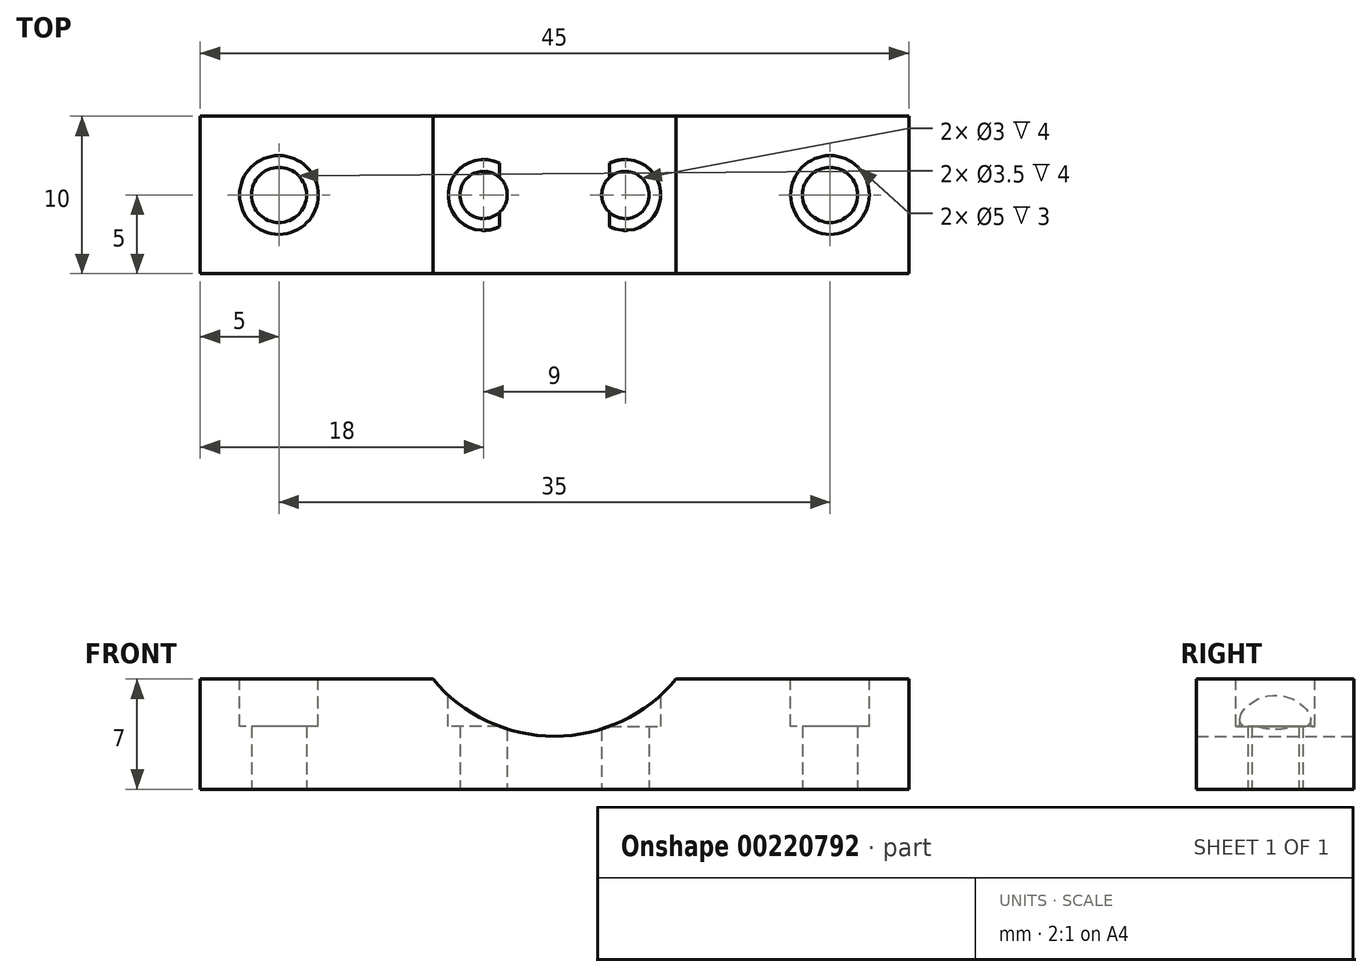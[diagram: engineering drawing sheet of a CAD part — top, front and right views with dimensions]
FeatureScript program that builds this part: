
annotation { "Feature Type Name" : "Feature", "Feature Type Description" : "" }
export const myFeature = defineFeature(function(context is Context, id is Id, definition is map)
    precondition{}
    {
        {
            var Q0;
            Q0=qCreatedBy(makeId("Top.planeOp"),FACE);
            var sketch = newSketch(context, id + "F0", { "sketchPlane" : qUnion([Q0])});
            skLineSegment(sketch, "E0.bottom", {"start": v(22.5, 5) * mm, "end": v(-22.5, 5) * mm});
            skLineSegment(sketch, "E0.top", {"start": v(22.5, -5) * mm, "end": v(-22.5, -5) * mm});
            skLineSegment(sketch, "E0.left", {"start": v(22.5, 5) * mm, "end": v(22.5, -5) * mm});
            skLineSegment(sketch, "E0.right", {"start": v(-22.5, 5) * mm, "end": v(-22.5, -5) * mm});
            skPoint(sketch, "E0.middle", {"position": v(0, 0) * mm});
            skCircle(sketch, "E1", {"center": v(-4.5, 0) * mm, "radius": 1.5 * mm});
            skCircle(sketch, "E2", {"center": v(4.5, 0) * mm, "radius": 1.5 * mm});
            skLineSegment(sketch, "E3", {"start": v(-22.5, 0) * mm, "end": v(-17.5, 0) * mm});
            skLineSegment(sketch, "E4", {"start": v(22.5, 0) * mm, "end": v(17.5, 0) * mm});
            skCircle(sketch, "E5", {"center": v(-17.5, 0) * mm, "radius": 1.75 * mm});
            skCircle(sketch, "E6", {"center": v(17.5, 0) * mm, "radius": 1.75 * mm});
            skSolve(sketch);
        }
        {
            var Q0;
            {var subQ3=sQuery(id+"F0.wireOp",EDGE,"E0.bottom");Q0=makeQuery(id+"F0.imprint","IMPRINT",FACE,{"disambiguationData":[TD([[makeQuery(id+"F0.imprint","IMPRINT",EDGE,{"derivedFrom":subQ3}),1.0]])]});}
            extrude(context, id + "F1", {"entities" : qUnion([Q0]), "depth" : 7 * mm});
        }
        {
            var Q0;
            Q0=makeQuery(id+"F1.opExtrude","CAP_FACE",FACE,{"disambiguationData":[OSD([sQuery(id+"F0.wireOp",EDGE,"E0.bottom"),sQuery(id+"F0.wireOp",EDGE,"E0.top"),sQuery(id+"F0.wireOp",EDGE,"E0.left"),sQuery(id+"F0.wireOp",EDGE,"E0.right"),sQuery(id+"F0.wireOp",EDGE,"E1"),sQuery(id+"F0.wireOp",EDGE,"E2"),sQuery(id+"F0.wireOp",EDGE,"E5"),sQuery(id+"F0.wireOp",EDGE,"E6")])],"isStart":false});
            var sketch = newSketch(context, id + "F2", { "sketchPlane" : qUnion([Q0])});
            skCircle(sketch, "E7", {"center": v(-17.5, 0) * mm, "radius": 2.5 * mm});
            skCircle(sketch, "E8", {"center": v(-4.5, 0) * mm, "radius": 2.25 * mm});
            skCircle(sketch, "E9", {"center": v(4.5, 0) * mm, "radius": 2.25 * mm});
            skCircle(sketch, "E10", {"center": v(17.5, 0) * mm, "radius": 2.5 * mm});
            skSolve(sketch);
        }
        {
            var Q0;
            Q0=makeQuery(id+"F2.imprint","IMPRINT",FACE,{"disambiguationData":[TD([[makeQuery(id+"F2.imprint","IMPRINT",EDGE,{"derivedFrom":sQuery(id+"F2.wireOp",EDGE,"E7")}),1.0]])]});
            var Q1;
            Q1=makeQuery(id+"F2.imprint","IMPRINT",FACE,{"disambiguationData":[TD([[makeQuery(id+"F2.imprint","IMPRINT",EDGE,{"derivedFrom":sQuery(id+"F2.wireOp",EDGE,"E8")}),1.0]])]});
            var Q2;
            Q2=makeQuery(id+"F2.imprint","IMPRINT",FACE,{"disambiguationData":[TD([[makeQuery(id+"F2.imprint","IMPRINT",EDGE,{"derivedFrom":sQuery(id+"F2.wireOp",EDGE,"E9")}),1.0]])]});
            var Q3;
            Q3=makeQuery(id+"F2.imprint","IMPRINT",FACE,{"disambiguationData":[TD([[makeQuery(id+"F2.imprint","IMPRINT",EDGE,{"derivedFrom":sQuery(id+"F2.wireOp",EDGE,"E10")}),1.0]])]});
            extrude(context, id + "F3", {"entities" : qUnion([Q0, Q1, Q2, Q3]), "operationType" : NewBodyOperationType.REMOVE, "oppositeDirection" : true, "depth" : 3 * mm});
        }
        {
            var Q0;
            Q0=makeQuery(id+"F1.opExtrude","SWEPT_FACE",FACE,{"disambiguationData":[OSD([sQuery(id+"F0.wireOp",EDGE,"E0.bottom")])]});
            var sketch = newSketch(context, id + "F4", { "sketchPlane" : qUnion([Q0])});
            skLineSegment(sketch, "E11", {"start": v(0, 7) * mm, "end": v(0, 13.42) * mm});
            skPoint(sketch, "E11.endSnap0", {"position": v(0, 7) * mm});
            skCircle(sketch, "E12", {"center": v(0, 13.42) * mm, "radius": 10.04 * mm});
            skSolve(sketch);
        }
        {
            var Q0;
            {var subQ1=makeQuery(id+"F1.opExtrude","CAP_EDGE",EDGE,{"disambiguationData":[OSD([sQuery(id+"F0.wireOp",EDGE,"E0.bottom")])],"isStart":false});var subQ4=makeQuery(id+"F4.imprint","IMPRINT",VERTEX,{"derivedFrom":subQ1});Q0=makeQuery(id+"F4.imprint","IMPRINT",FACE,{"disambiguationData":[TD([[makeQuery(id+"F4.imprint","IMPRINT",EDGE,{"disambiguationData":[TD([[subQ4,1.0]])],"derivedFrom":subQ1}),1.0]])]});}
            var Q1;
            {var subQ1=makeQuery(id+"F1.opExtrude","CAP_EDGE",EDGE,{"disambiguationData":[OSD([sQuery(id+"F0.wireOp",EDGE,"E0.bottom")])],"isStart":false});var subQ4=makeQuery(id+"F4.imprint","IMPRINT",VERTEX,{"derivedFrom":subQ1});Q1=makeQuery(id+"F4.imprint","IMPRINT",FACE,{"disambiguationData":[TD([[makeQuery(id+"F4.imprint","IMPRINT",EDGE,{"disambiguationData":[TD([[subQ4,1.0]])],"derivedFrom":subQ1}),-1.0]])]});}
            extrude(context, id + "F5", {"entities" : qUnion([Q0, Q1]), "operationType" : NewBodyOperationType.REMOVE, "oppositeDirection" : true, "depth" : 25 * mm});
        }
    });
